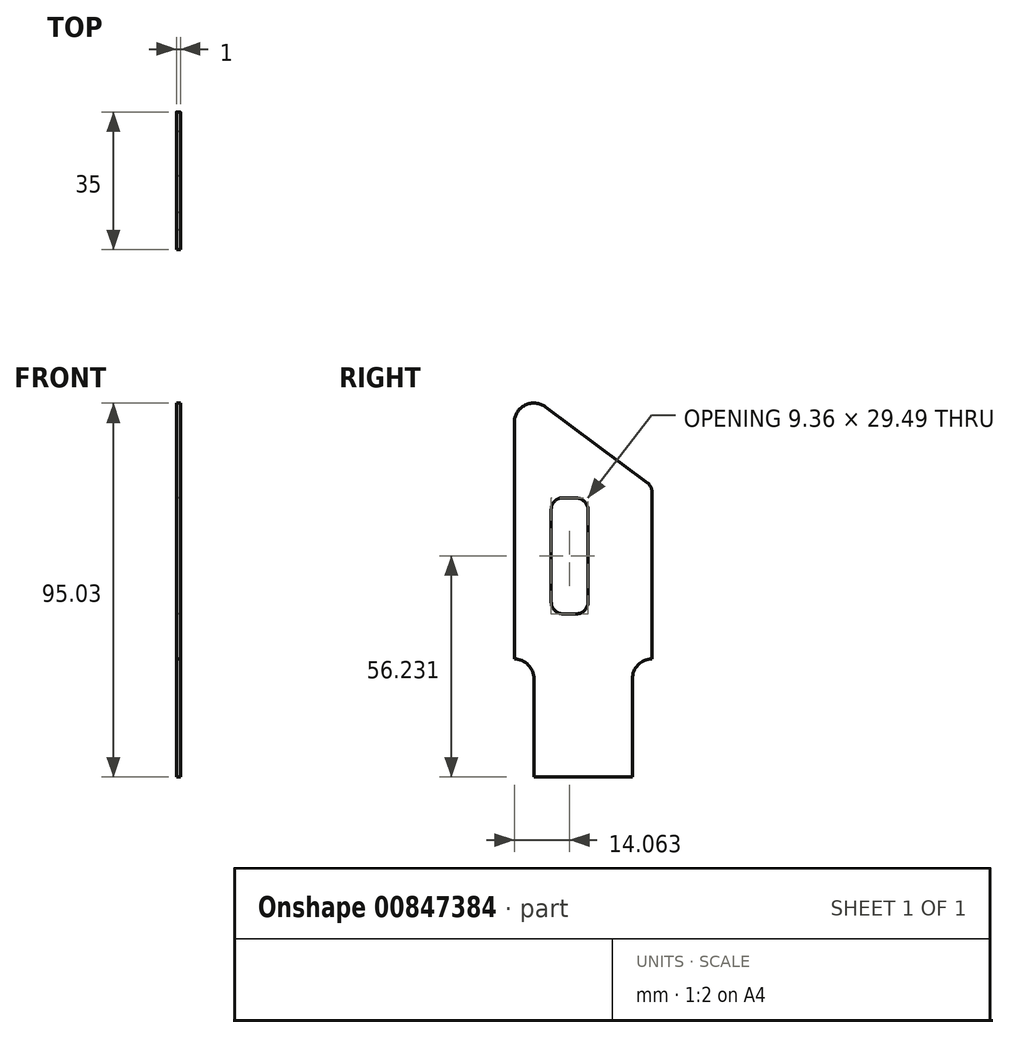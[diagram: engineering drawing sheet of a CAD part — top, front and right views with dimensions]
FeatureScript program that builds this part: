
annotation { "Feature Type Name" : "Feature", "Feature Type Description" : "" }
export const myFeature = defineFeature(function(context is Context, id is Id, definition is map)
    precondition{}
    {
        {
            var Q0;
            Q0=qCreatedBy(makeId("Right.planeOp"),FACE);
            var sketch = newSketch(context, id + "F0", { "sketchPlane" : qUnion([Q0])});
            skLineSegment(sketch, "E0", {"start": v(-62.16, -58.83) * mm, "end": v(-62.16, -33.83) * mm});
            skLineSegment(sketch, "E1", {"start": v(-62.16, -58.83) * mm, "end": v(-37.16, -58.83) * mm});
            skLineSegment(sketch, "E2", {"start": v(-37.16, -58.83) * mm, "end": v(-37.16, -33.83) * mm});
            skLineSegment(sketch, "E3", {"start": v(-32.16, -28.83) * mm, "end": v(-32.16, -28.83) * mm});
            skLineSegment(sketch, "E4", {"start": v(-67.16, -28.83) * mm, "end": v(-67.16, -28.83) * mm});
            skPoint(sketch, "E5.visualSharp", {"position": v(-37.16, -28.83) * mm});
            skArc(sketch, "E5.filletArc", {"start": v(-32.16, -28.83) * mm, "mid": v(-35.7, -30.3) * mm, "end": v(-37.16, -33.83) * mm});
            skPoint(sketch, "E6.visualSharp", {"position": v(-62.16, -28.83) * mm});
            skArc(sketch, "E6.filletArc", {"start": v(-62.16, -33.83) * mm, "mid": v(-63.62, -30.3) * mm, "end": v(-67.16, -28.83) * mm});
            skLineSegment(sketch, "E7", {"start": v(-67.16, -28.83) * mm, "end": v(-67.16, 31.2) * mm});
            skLineSegment(sketch, "E8", {"start": v(-32.16, -28.83) * mm, "end": v(-32.16, 13.54) * mm});
            skLineSegment(sketch, "E9", {"start": v(-59.17, 35.2) * mm, "end": v(-33.37, 15.95) * mm});
            skPoint(sketch, "E10.visualSharp", {"position": v(-67.16, 41.17) * mm});
            skArc(sketch, "E10.filletArc", {"start": v(-59.17, 35.2) * mm, "mid": v(-64.4, 35.67) * mm, "end": v(-67.16, 31.2) * mm});
            skPoint(sketch, "E11.visualSharp", {"position": v(-32.16, 15.05) * mm});
            skArc(sketch, "E11.filletArc", {"start": v(-32.16, 13.54) * mm, "mid": v(-32.48, 14.89) * mm, "end": v(-33.37, 15.95) * mm});
            skSolve(sketch);
        }
        {
            var Q0;
            Q0=qCreatedBy(makeId("Right.planeOp"),FACE);
            var sketch = newSketch(context, id + "F1", { "sketchPlane" : qUnion([Q0])});
            skLineSegment(sketch, "E12", {"start": v(-57.78, 9.15) * mm, "end": v(-57.78, -14.34) * mm});
            skLineSegment(sketch, "E13", {"start": v(-54.78, -17.34) * mm, "end": v(-51.42, -17.34) * mm});
            skLineSegment(sketch, "E14", {"start": v(-48.42, -14.34) * mm, "end": v(-48.42, 9.06) * mm});
            skLineSegment(sketch, "E15", {"start": v(-51.34, 12.06) * mm, "end": v(-54.7, 12.15) * mm});
            skPoint(sketch, "E16.visualSharp", {"position": v(-57.78, 12.23) * mm});
            skArc(sketch, "E16.filletArc", {"start": v(-54.7, 12.15) * mm, "mid": v(-56.87, 11.3) * mm, "end": v(-57.78, 9.15) * mm});
            skPoint(sketch, "E17.visualSharp", {"position": v(-48.42, 11.98) * mm});
            skArc(sketch, "E17.filletArc", {"start": v(-48.42, 9.06) * mm, "mid": v(-49.27, 11.15) * mm, "end": v(-51.34, 12.06) * mm});
            skPoint(sketch, "E18.visualSharp", {"position": v(-48.42, -17.34) * mm});
            skArc(sketch, "E18.filletArc", {"start": v(-51.42, -17.34) * mm, "mid": v(-49.3, -16.46) * mm, "end": v(-48.42, -14.34) * mm});
            skPoint(sketch, "E19.visualSharp", {"position": v(-57.78, -17.34) * mm});
            skArc(sketch, "E19.filletArc", {"start": v(-57.78, -14.34) * mm, "mid": v(-56.9, -16.46) * mm, "end": v(-54.78, -17.34) * mm});
            skSolve(sketch);
        }
        {
            var Q0;
            Q0=makeQuery(id+"F0.imprint","IMPRINT",FACE,{"disambiguationData":[TD([[makeQuery(id+"F0.imprint","IMPRINT",EDGE,{"derivedFrom":sQuery(id+"F0.wireOp",EDGE,"E0")}),-1.0]])]});
            extrude(context, id + "F2", {"entities" : qUnion([Q0]), "depth" : 1 * mm, "offsetDistance" : 25 * mm});
        }
        {
            var Q0;
            Q0 = qSketchRegion(id + "F1", true);
            extrude(context, id + "F3", {"entities" : qUnion([Q0]), "operationType" : NewBodyOperationType.REMOVE, "depth" : 1 * mm, "offsetDistance" : 25 * mm});
        }
    });
